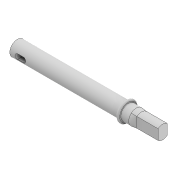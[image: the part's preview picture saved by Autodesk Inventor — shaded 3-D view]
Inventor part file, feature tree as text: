
AUTODESK INVENTOR PART (.ipt)
format: ipt  version: 2022 (Build 260153000, 153)  size: 160,256 bytes
history: native  units: mm
features: extrude x5, sketch x5, other x3, plane x2, fillet x2, projected_geometry x2, loft x1, chamfer x1
ambient origin geometry x8: Origin, YZ Plane, XZ Plane, XY Plane, X Axis, Y Axis, Z Axis, Center Point
bodies: Solid1 (feature_tree)
feature tree (21):
  extrude  "Shaft"  Depth=2.35mm TaperAngle=0.0deg
  extrude  "Slot"  Depth=2.0mm
  plane  "Work Plane1"
  extrude  "Wheel Inert Profile"  Depth=1.0mm
  other  "Offset for Wheel"
  loft  "Loft1"
  plane  "Work Plane2"
  extrude  "Stopper"  Depth=0.5mm
  fillet  "Fillet1"  Radius=2.0mm
  extrude  "Offset"  TaperAngle=0.0deg  [1 undecoded]
  fillet  "Fillet2"  [1 undecoded]
  chamfer  "Chamfer1"  [1 undecoded]
  sketch  "Sketch1"  dims[d2=0.0mm d9=2.35mm d10=0.0mm]
  sketch  "Sketch2"  dims[d17=1.8mm d20=2.0mm]
  sketch  "Sketch3"  dims[d21=1.0mm d22=7.0mm]
  other  "Edges1"
  other  "Edges2"
  sketch  "Sketch4"  dims[d23=5.5mm d24=4.0mm]
  sketch  "Sketch5"  dims[d25=8.0mm d26=0.0mm d27=0.15mm d28=0.1mm d29=2.0mm d30=0.0mm d31=90.0deg d32=0.0mm d33=90.0deg d34=-41.0mm d35=7.5mm d36=1.0mm d37=0.0mm d38=0.5mm d42=9.0mm d43=0.0mm d44=0.5mm d45=0.5mm d46=2.0mm d47=45.0deg d48=5.3mm]
  projected_geometry  "Project Cut Edges1"
  projected_geometry  "Project Cut Edges2"
note: 3 required parameter values undecoded (feature->parameter linkage not recoverable at this tier; creation-order binding heuristic only, values carry confidence <= 0.55)
